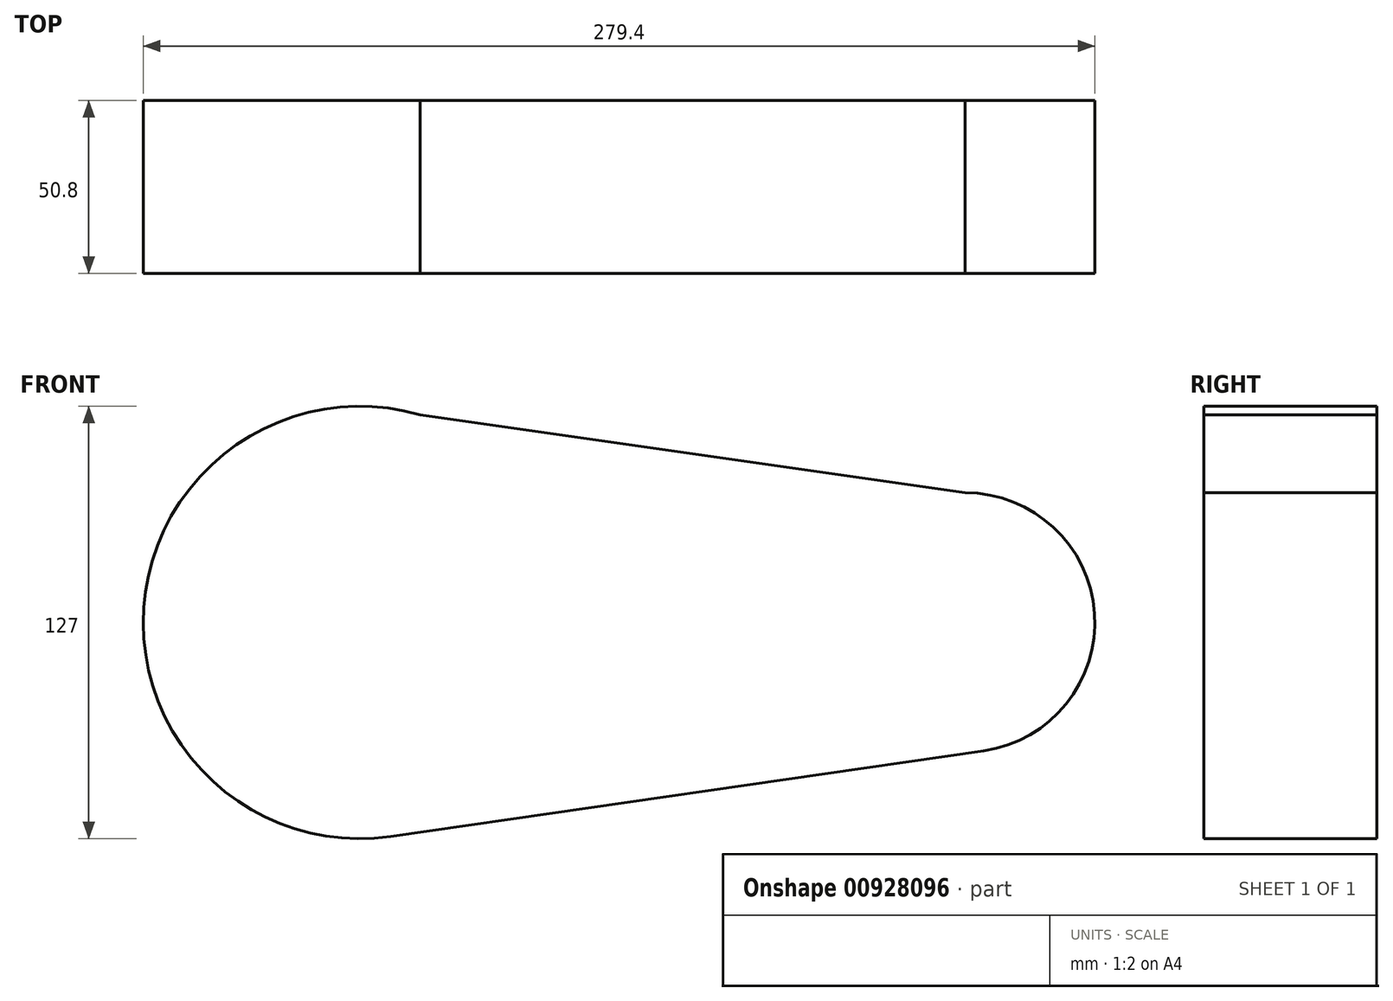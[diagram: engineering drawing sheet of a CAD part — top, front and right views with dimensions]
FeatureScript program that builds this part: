
annotation { "Feature Type Name" : "Feature", "Feature Type Description" : "" }
export const myFeature = defineFeature(function(context is Context, id is Id, definition is map)
    precondition{}
    {
        {
            var Q0;
            Q0=qCreatedBy(makeId("Front.planeOp"),FACE);
            var sketch = newSketch(context, id + "F0", { "sketchPlane" : qUnion([Q0])});
            skCircle(sketch, "E0", {"center": v(0, 0) * mm, "radius": 63.5 * mm});
            skCircle(sketch, "E1", {"center": v(177.8, 0) * mm, "radius": 38.1 * mm});
            skLineSegment(sketch, "E2", {"start": v(9.1, -62.85) * mm, "end": v(183.24, -37.7) * mm});
            skLineSegment(sketch, "E3", {"start": v(0, 63.5) * mm, "end": v(177.8, 38.1) * mm});
            skSolve(sketch);
        }
        {
            var Q0;
            Q0 = qSketchRegion(id + "F0", true);
            extrude(context, id + "F1", {"entities" : qUnion([Q0]), "depth" : 50.8 * mm, "offsetDistance" : 25.4 * mm});
        }
        {
            var Q0;
            Q0=sQuery(id+"F0.wireOp",EDGE,"E0");
            extrude(context, id + "F2", {"bodyType" : ToolBodyType.SURFACE, "surfaceEntities" : qUnion([Q0]), "endBound" : BoundingType.SYMMETRIC, "depth" : 76.2 * mm, "offsetDistance" : 25.4 * mm});
        }
    });
